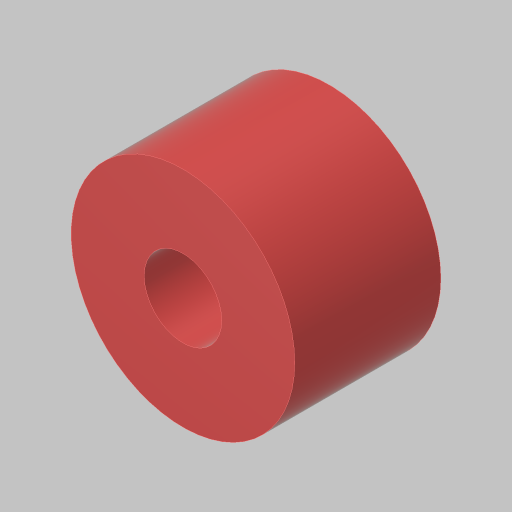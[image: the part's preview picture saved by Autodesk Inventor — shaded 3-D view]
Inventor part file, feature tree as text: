
AUTODESK INVENTOR PART (.ipt)
format: ipt  version: 2023.5 (Build 275446000, 446)  size: 112,128 bytes
history: native  units: in
note: dims shown in document units (in); Inventor stores cm internally (conversion verified against a paired STEP export)
features: extrude x1, sketch x1
ambient origin geometry x8: Origin, YZ Plane, XZ Plane, XY Plane, X Axis, Y Axis, Z Axis, Center Point
bodies: Solid1 (feature_tree)
feature tree (2):
  extrude  "Extrusion1"  Depth=0.49in
  sketch  "Sketch1"  dims[d0=0.75in d1=0.26in d2=0.49in d3=0.0in]
